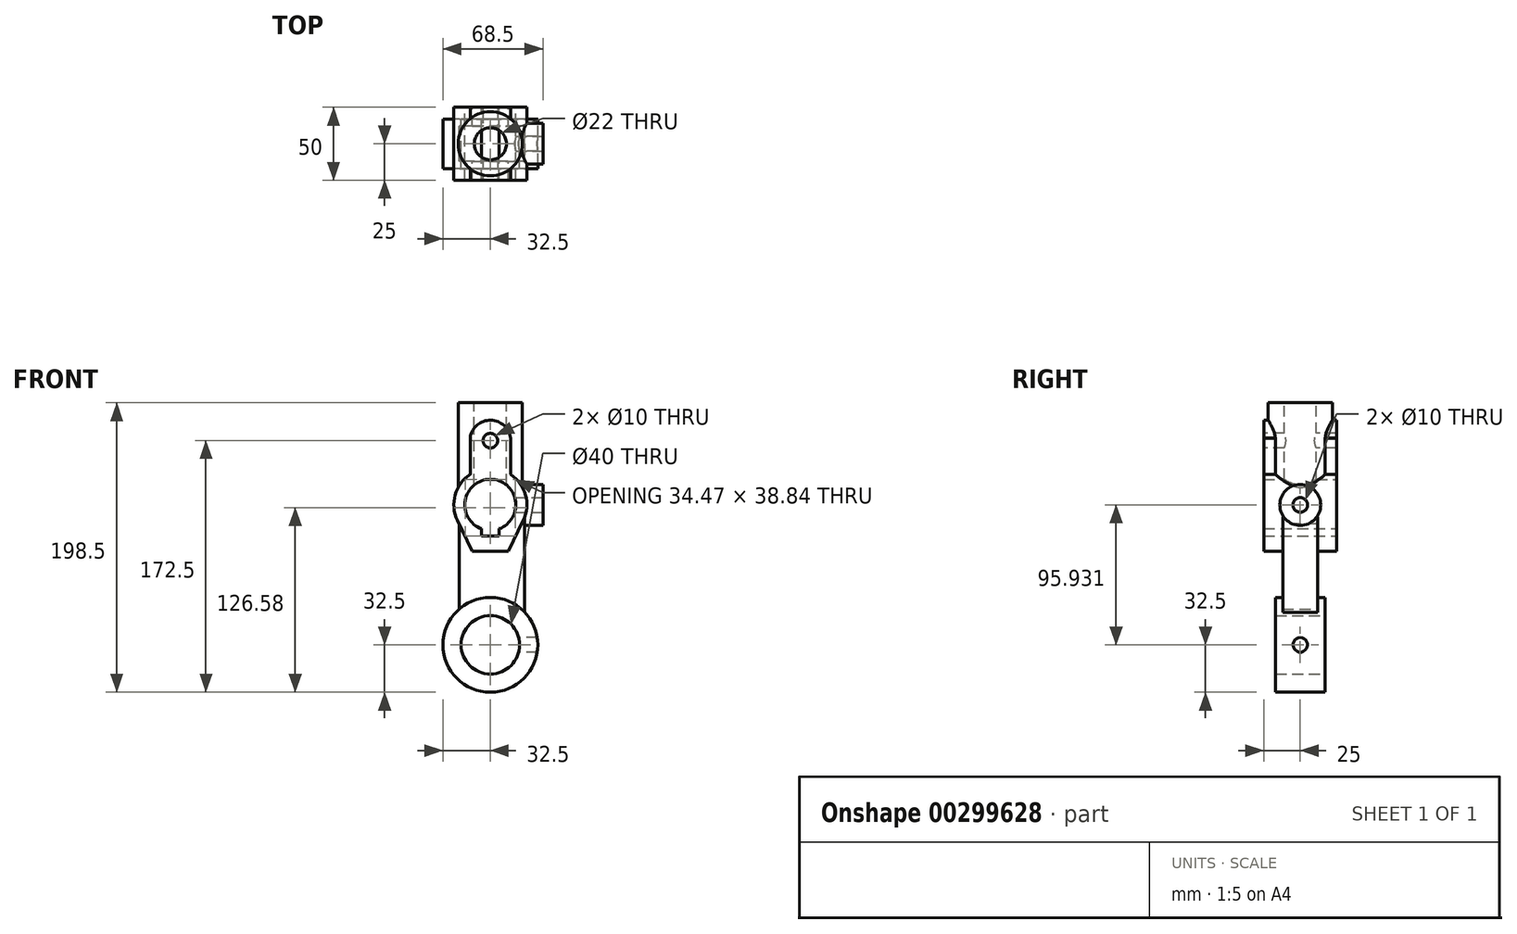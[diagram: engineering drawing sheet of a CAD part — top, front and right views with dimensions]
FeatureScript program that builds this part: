
annotation { "Feature Type Name" : "Feature", "Feature Type Description" : "" }
export const myFeature = defineFeature(function(context is Context, id is Id, definition is map)
    precondition{}
    {
        {
            var Q0;
            Q0=qCreatedBy(makeId("Front.planeOp"),FACE);
            var sketch = newSketch(context, id + "F0", { "sketchPlane" : qUnion([Q0])});
            skCircle(sketch, "E0", {"center": v(0, 0) * mm, "radius": 20 * mm});
            skCircle(sketch, "E1", {"center": v(0, 0) * mm, "radius": 32.5 * mm});
            skSolve(sketch);
        }
        {
            var Q0;
            Q0=makeQuery(id+"F0.imprint","IMPRINT",FACE,{"disambiguationData":[TD([[makeQuery(id+"F0.imprint","IMPRINT",EDGE,{"derivedFrom":sQuery(id+"F0.wireOp",EDGE,"E0")}),-1.0]])]});
            extrude(context, id + "F1", {"entities" : qUnion([Q0]), "endBound" : BoundingType.SYMMETRIC, "depth" : 34 * mm});
        }
        {
            var Q0;
            Q0=qCreatedBy(makeId("Right.planeOp"),FACE);
            var sketch = newSketch(context, id + "F2", { "sketchPlane" : qUnion([Q0])});
            skCircle(sketch, "E2", {"center": v(0, 0) * mm, "radius": 5 * mm});
            skSolve(sketch);
        }
        {
            var Q0;
            Q0 = qSketchRegion(id + "F2", true);
            extrude(context, id + "F3", {"entities" : qUnion([Q0]), "operationType" : NewBodyOperationType.REMOVE, "endBound" : BoundingType.THROUGH_ALL, "depth" : 50 * mm});
        }
        {
            var Q0;
            Q0=qCreatedBy(makeId("Front.planeOp"),FACE);
            var sketch = newSketch(context, id + "F4", { "sketchPlane" : qUnion([Q0])});
            skLineSegment(sketch, "E3", {"start": v(0, 0) * mm, "end": v(0, 96) * mm, "construction": true});
            skCircle(sketch, "E4", {"center": v(0, 96) * mm, "radius": 17.5 * mm});
            skCircle(sketch, "E5", {"center": v(0, 96) * mm, "radius": 25 * mm});
            skLineSegment(sketch, "E6", {"start": v(-6, 79.56) * mm, "end": v(-6, 74.66) * mm});
            skLineSegment(sketch, "E7", {"start": v(-6, 74.66) * mm, "end": v(6, 74.66) * mm});
            skLineSegment(sketch, "E8", {"start": v(6, 74.66) * mm, "end": v(6, 79.56) * mm});
            skPoint(sketch, "E9", {"position": v(0, 64) * mm});
            skLineSegment(sketch, "E10", {"start": v(-12.5, 64) * mm, "end": v(12.5, 64) * mm});
            skLineSegment(sketch, "E11", {"start": v(12.5, 64) * mm, "end": v(22.6, 85.3) * mm});
            skLineSegment(sketch, "E12", {"start": v(-12.5, 64) * mm, "end": v(-22.6, 85.3) * mm});
            skSolve(sketch);
        }
        {
            var Q0;
            {var subQ0=sQuery(id+"F4.wireOp",EDGE,"E6");Q0=makeQuery(id+"F4.imprint","IMPRINT",FACE,{"disambiguationData":[TD([[makeQuery(id+"F4.imprint","IMPRINT",EDGE,{"derivedFrom":subQ0}),-1.0]])]});}
            var Q1;
            Q1=makeQuery(id+"F4.imprint","IMPRINT",FACE,{"disambiguationData":[TD([[makeQuery(id+"F4.imprint","IMPRINT",EDGE,{"derivedFrom":sQuery(id+"F4.wireOp",EDGE,"E10")}),1.0]])]});
            extrude(context, id + "F5", {"entities" : qUnion([Q0, Q1]), "endBound" : BoundingType.SYMMETRIC, "depth" : 50 * mm});
        }
        {
            var Q0;
            Q0=qCreatedBy(makeId("Right.planeOp"),FACE);
            cPlane(context, id + "F6", {"entities" : qUnion([Q0]), "cplaneType" : CPlaneType.OFFSET, "offset" : 36 * mm, "width" : 150 * mm, "height" : 150 * mm});
        }
        {
            var Q0;
            Q0=qCreatedBy(id+"F6.planeOp",FACE);
            var sketch = newSketch(context, id + "F7", { "sketchPlane" : qUnion([Q0])});
            skCircle(sketch, "E13", {"center": v(0, 95.93) * mm, "radius": 14 * mm});
            skCircle(sketch, "E14", {"center": v(0, 95.93) * mm, "radius": 5 * mm});
            skSolve(sketch);
        }
        {
            var Q0;
            Q0 = qSketchRegion(id + "F7", true);
            extrude(context, id + "F8", {"entities" : qUnion([Q0]), "operationType" : NewBodyOperationType.ADD, "oppositeDirection" : true, "depth" : 25 * mm});
        }
        {
            var Q0;
            {var subQ0=sQuery(id+"F4.wireOp",EDGE,"E4");var subQ1=makeQuery(id+"F4.imprint","INTERSECT",VERTEX,{"derivedFrom":[subQ0,sQuery(id+"F4.wireOp",EDGE,"E6")]});Q0=makeQuery(id+"F4.imprint","IMPRINT",FACE,{"disambiguationData":[TD([[makeQuery(id+"F4.imprint","IMPRINT",EDGE,{"disambiguationData":[TD([[subQ1,-1.0]])],"derivedFrom":subQ0}),1.0]])]});}
            var sketch = newSketch(context, id + "F9", { "sketchPlane" : qUnion([Q0])});
            skCircle(sketch, "E15", {"center": v(0, 96) * mm, "radius": 17.5 * mm});
            skSolve(sketch);
        }
        {
            var Q0;
            Q0=makeQuery(id+"F5.opExtrude","CAP_FACE",FACE,{"disambiguationData":[OSD([sQuery(id+"F4.wireOp",EDGE,"E4"),sQuery(id+"F4.wireOp",EDGE,"E5"),sQuery(id+"F4.wireOp",EDGE,"E6"),sQuery(id+"F4.wireOp",EDGE,"E7"),sQuery(id+"F4.wireOp",EDGE,"E8"),sQuery(id+"F4.wireOp",EDGE,"E10"),sQuery(id+"F4.wireOp",EDGE,"E11"),sQuery(id+"F4.wireOp",EDGE,"E12")])],"isStart":false});
            var sketch = newSketch(context, id + "F10", { "sketchPlane" : qUnion([Q0])});
            skCircle(sketch, "E16", {"center": v(0, 96) * mm, "radius": 17.5 * mm});
            skLineSegment(sketch, "E17", {"start": v(0, 96) * mm, "end": v(0, 140) * mm, "construction": true});
            skPoint(sketch, "E17.endSnap0", {"position": v(0, 121) * mm});
            skCircle(sketch, "E18", {"center": v(0, 140) * mm, "radius": 5 * mm});
            skArc(sketch, "E19", {"start": v(13.9, 141.7) * mm, "mid": v(0.25, 154) * mm, "end": v(-13.83, 142.2) * mm});
            skLineSegment(sketch, "E20", {"start": v(-13.83, 142.2) * mm, "end": v(-13.83, 116.83) * mm});
            skLineSegment(sketch, "E21", {"start": v(13.9, 141.7) * mm, "end": v(13.9, 116.78) * mm});
            skSolve(sketch);
        }
        {
            var Q0;
            Q0=qCreatedBy(makeId("Front.planeOp"),FACE);
            var sketch = newSketch(context, id + "F11", { "sketchPlane" : qUnion([Q0])});
            skLineSegment(sketch, "E22", {"start": v(-21.44, 0) * mm, "end": v(23.56, 0) * mm});
            skLineSegment(sketch, "E23", {"start": v(23.56, 0) * mm, "end": v(23.56, 96) * mm});
            skLineSegment(sketch, "E24", {"start": v(23.56, 96) * mm, "end": v(-21.44, 96) * mm});
            skLineSegment(sketch, "E25", {"start": v(-21.44, 96) * mm, "end": v(-21.44, 0) * mm});
            skCircle(sketch, "E26", {"center": v(0, 96) * mm, "radius": 17.5 * mm});
            skPoint(sketch, "E26.centerSnap0", {"position": v(1.06, 96) * mm});
            skCircle(sketch, "E27", {"center": v(0, 0) * mm, "radius": 32.5 * mm});
            skCircle(sketch, "E28", {"center": v(0, 96) * mm, "radius": 25 * mm});
            skSolve(sketch);
        }
        {
            var Q0;
            {var subQ0=sQuery(id+"F11.wireOp",EDGE,"E27");var subQ1=sQuery(id+"F11.wireOp",EDGE,"E23");var subQ2=makeQuery(id+"F11.imprint","INTERSECT",VERTEX,{"derivedFrom":[subQ1,subQ0]});Q0=makeQuery(id+"F11.imprint","IMPRINT",FACE,{"disambiguationData":[TD([[makeQuery(id+"F11.imprint","IMPRINT",EDGE,{"disambiguationData":[TD([[subQ2,-1.0]])],"derivedFrom":subQ1}),1.0]])]});}
            extrude(context, id + "F12", {"entities" : qUnion([Q0]), "operationType" : NewBodyOperationType.ADD, "endBound" : BoundingType.SYMMETRIC, "depth" : 24 * mm});
        }
        {
            var Q0;
            Q0=makeQuery(id+"F10.imprint","IMPRINT",FACE,{"disambiguationData":[TD([[makeQuery(id+"F10.imprint","IMPRINT",EDGE,{"derivedFrom":sQuery(id+"F10.wireOp",EDGE,"E18")}),-1.0]])]});
            var sketch = newSketch(context, id + "F13", { "sketchPlane" : qUnion([Q0])});
            skSolve(sketch);
        }
        {
            var Q0;
            Q0 = qSketchRegion(id + "F13", true);
            var Q1;
            Q1=makeQuery(id+"F10.imprint","IMPRINT",FACE,{"disambiguationData":[TD([[makeQuery(id+"F10.imprint","IMPRINT",EDGE,{"derivedFrom":sQuery(id+"F10.wireOp",EDGE,"E18")}),-1.0]])]});
            extrude(context, id + "F14", {"entities" : qUnion([Q0, Q1]), "operationType" : NewBodyOperationType.ADD, "oppositeDirection" : true, "depth" : 50 * mm});
        }
        {
            var Q0;
            Q0=qCreatedBy(makeId("Top.planeOp"),FACE);
            cPlane(context, id + "F15", {"entities" : qUnion([Q0]), "cplaneType" : CPlaneType.OFFSET, "offset" : 166 * mm, "width" : 150 * mm, "height" : 150 * mm});
        }
        {
            var Q0;
            Q0=qCreatedBy(id+"F15.planeOp",FACE);
            var sketch = newSketch(context, id + "F16", { "sketchPlane" : qUnion([Q0])});
            skCircle(sketch, "E29", {"center": v(0, 0) * mm, "radius": 11 * mm});
            skCircle(sketch, "E30", {"center": v(0, 0) * mm, "radius": 22 * mm});
            skSolve(sketch);
        }
        {
            var Q0;
            Q0=makeQuery(id+"F16.imprint","IMPRINT",FACE,{"disambiguationData":[TD([[makeQuery(id+"F16.imprint","IMPRINT",EDGE,{"derivedFrom":sQuery(id+"F16.wireOp",EDGE,"E29")}),-1.0]])]});
            extrude(context, id + "F17", {"entities" : qUnion([Q0]), "operationType" : NewBodyOperationType.ADD, "oppositeDirection" : true, "depth" : 70 * mm});
        }
        {
            var Q0;
            {var subQ0=sQuery(id+"F9.wireOp",EDGE,"E15");var subQ1=makeQuery(id+"F9.imprint","IMPRINT",VERTEX,{"disambiguationData":[OD(0.0)],"derivedFrom":subQ0});Q0=makeQuery(id+"F9.imprint","IMPRINT",FACE,{"disambiguationData":[TD([[makeQuery(id+"F9.imprint","IMPRINT",EDGE,{"disambiguationData":[TD([[subQ1,-1.0]])],"derivedFrom":subQ0}),1.0]])]});}
            extrude(context, id + "F18", {"entities" : qUnion([Q0]), "operationType" : NewBodyOperationType.REMOVE, "endBound" : BoundingType.SYMMETRIC, "oppositeDirection" : true, "depth" : 50 * mm});
        }
        {
            var Q0;
            Q0=makeQuery(id+"F8.opExtrude","CAP_FACE",FACE,{"disambiguationData":[OSD([sQuery(id+"F7.wireOp",EDGE,"E13"),sQuery(id+"F7.wireOp",EDGE,"E14")])],"isStart":true});
            var sketch = newSketch(context, id + "F19", { "sketchPlane" : qUnion([Q0])});
            skCircle(sketch, "E31", {"center": v(0, 95.93) * mm, "radius": 5 * mm});
            skSolve(sketch);
        }
        {
            var Q0;
            Q0 = qSketchRegion(id + "F19", true);
            extrude(context, id + "F20", {"entities" : qUnion([Q0]), "operationType" : NewBodyOperationType.REMOVE, "oppositeDirection" : true, "depth" : 25 * mm});
        }
        {
            var Q0;
            Q0=makeQuery(id+"F13.imprint","IMPRINT",FACE,{"disambiguationData":[TD([[makeQuery(id+"F13.imprint","IMPRINT",EDGE,{"derivedFrom":makeQuery(id+"F10.imprint","IMPRINT",EDGE,{"derivedFrom":sQuery(id+"F10.wireOp",EDGE,"E18")})}),1.0]])]});
            var sketch = newSketch(context, id + "F21", { "sketchPlane" : qUnion([Q0])});
            skCircle(sketch, "E32", {"center": v(0, 140) * mm, "radius": 5 * mm});
            skSolve(sketch);
        }
        {
            var Q0;
            Q0 = qSketchRegion(id + "F21", true);
            extrude(context, id + "F22", {"entities" : qUnion([Q0]), "operationType" : NewBodyOperationType.REMOVE, "endBound" : BoundingType.THROUGH_ALL, "oppositeDirection" : true, "depth" : 25 * mm});
        }
        {
            var Q0;
            Q0=makeQuery(id+"F17.opExtrude","CAP_FACE",FACE,{"disambiguationData":[OSD([sQuery(id+"F16.wireOp",EDGE,"E29"),sQuery(id+"F16.wireOp",EDGE,"E30")])],"isStart":true});
            var sketch = newSketch(context, id + "F23", { "sketchPlane" : qUnion([Q0])});
            skCircle(sketch, "E33", {"center": v(0, 0) * mm, "radius": 11 * mm});
            skSolve(sketch);
        }
        {
            var Q0;
            Q0 = qSketchRegion(id + "F23", true);
            extrude(context, id + "F24", {"entities" : qUnion([Q0]), "operationType" : NewBodyOperationType.REMOVE, "oppositeDirection" : true, "depth" : 60 * mm});
        }
    });
